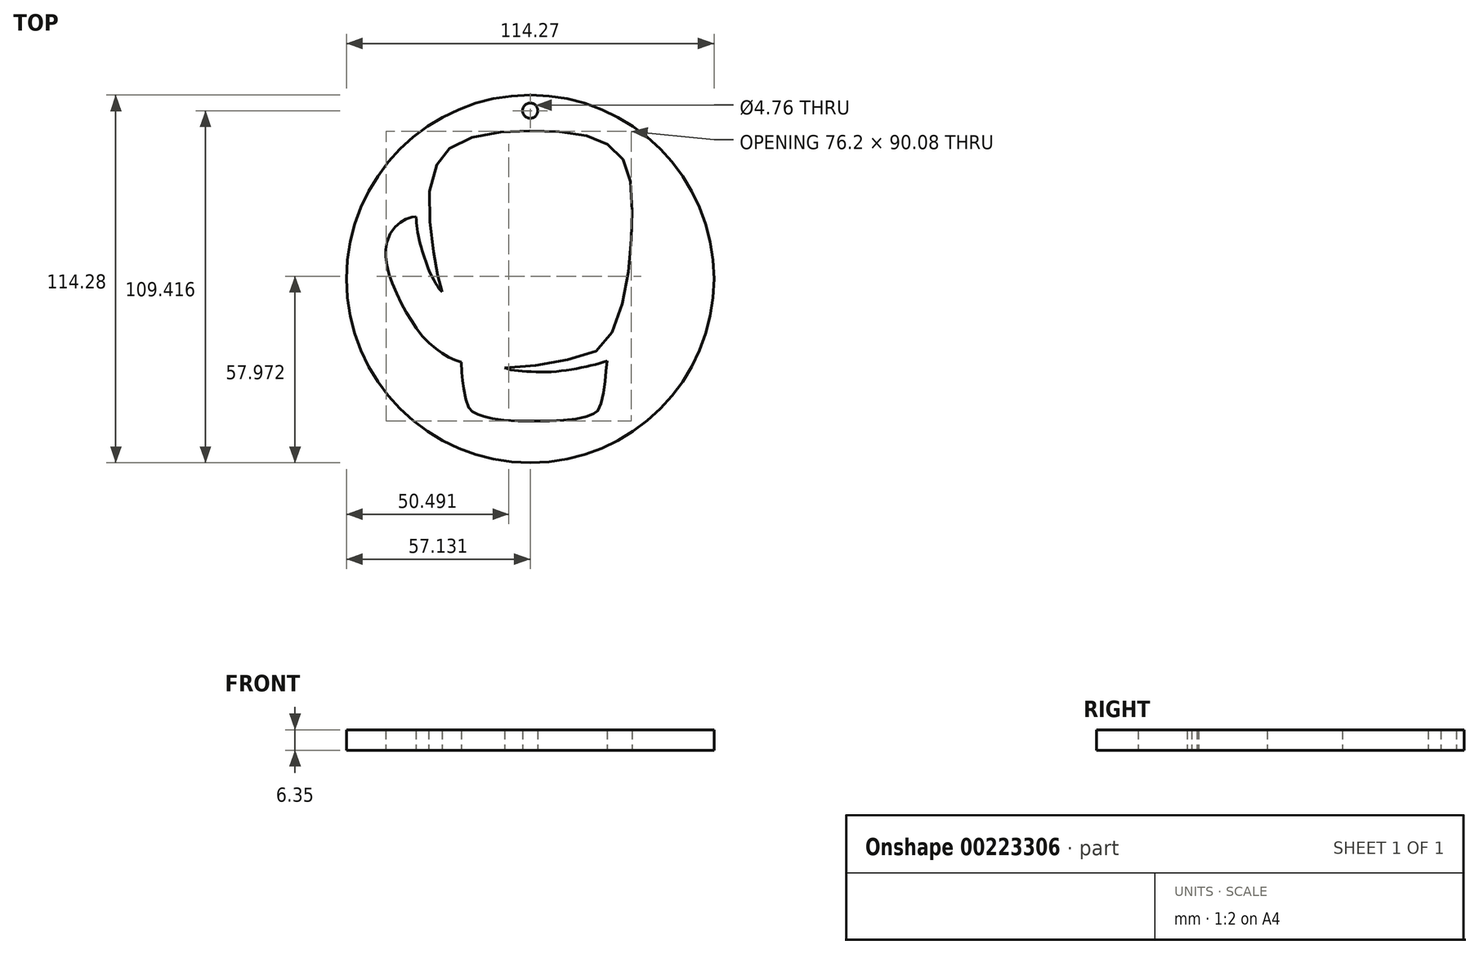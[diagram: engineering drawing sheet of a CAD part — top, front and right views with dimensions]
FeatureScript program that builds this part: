
annotation { "Feature Type Name" : "Feature", "Feature Type Description" : "" }
export const myFeature = defineFeature(function(context is Context, id is Id, definition is map)
    precondition{}
    {
        {
            var Q0;
            Q0=qCreatedBy(makeId("Top.planeOp"),FACE);
            var sketch = newSketch(context, id + "F0", { "sketchPlane" : qUnion([Q0])});
            skFitSpline(sketch, "E0", {"points": [v(-19.83, -27.64) * mm, v(-16.82, -28.45) * mm, v(-12.35, -28.83) * mm, v(-5.72, -28.9) * mm, v(1.21, -28.08) * mm, v(7.55, -26.81) * mm, v(12.02, -25.47) * mm], "startDerivative": vector(17.29, -8.64) * mm, "endDerivative": vector(27.03, 8.83) * mm});
            skFitSpline(sketch, "E1", {"points": [v(12.02, -25.47) * mm, v(11.52, -30.62) * mm, v(10.6, -36.69) * mm, v(9.34, -40.68) * mm, v(8.42, -41.6) * mm, v(6.65, -42.45) * mm, v(1.3, -43.69) * mm, v(-8.14, -44.22) * mm, v(-19.75, -43.9) * mm, v(-25.24, -43.07) * mm, v(-27.55, -42.4) * mm, v(-29.27, -41.56) * mm, v(-30.51, -40.72) * mm, v(-31.53, -38.6) * mm, v(-32.64, -33.36) * mm, v(-33, -30.44) * mm, v(-33.3, -25.93) * mm], "startDerivative": vector(-5.92, -73.94) * mm, "endDerivative": vector(-1.98, 80.2) * mm});
            skFitSpline(sketch, "E2", {"points": [v(-33.3, -25.93) * mm, v(-35.71, -25.04) * mm, v(-38.6, -23.54) * mm, v(-41.55, -21.45) * mm, v(-45.47, -17.7) * mm, v(-48.62, -13.22) * mm, v(-51.57, -8.28) * mm, v(-54.53, -1.8) * mm, v(-56.29, 3.44) * mm, v(-56.82, 7.75) * mm, v(-56.52, 10.97) * mm, v(-54.73, 15.08) * mm, v(-52.5, 17.3) * mm, v(-50.21, 18.74) * mm, v(-48.12, 19.27) * mm, v(-47.35, 19.26) * mm], "startDerivative": vector(-42.85, 14.66) * mm, "endDerivative": vector(20.25, -1.4) * mm});
            skFitSpline(sketch, "E3", {"points": [v(-47.35, 19.26) * mm, v(-47.23, 17.28) * mm, v(-46.89, 14.87) * mm, v(-46.24, 11.54) * mm, v(-45.35, 8.38) * mm, v(-44.33, 5.29) * mm, v(-42.94, 1.78) * mm, v(-41.1, -1.65) * mm, v(-40.08, -3.24) * mm, v(-39.3, -4.02) * mm], "startDerivative": vector(0.97, -20.52) * mm, "endDerivative": vector(11.11, -9.93) * mm});
            skFitSpline(sketch, "E4", {"points": [v(-39.3, -4.02) * mm, v(-39.64, -2.67) * mm, v(-40.4, 0) * mm, v(-40.97, 3.02) * mm, v(-41.79, 7.52) * mm, v(-42.61, 14.6) * mm, v(-43.35, 21.14) * mm, v(-42.98, 28.51) * mm, v(-41.35, 34.47) * mm, v(-39.68, 37.48) * mm, v(-37.55, 40.04) * mm, v(-34.2, 42.37) * mm, v(-28.98, 44.27) * mm, v(-22.63, 45.45) * mm, v(-16.36, 45.84) * mm, v(-9.33, 45.96) * mm, v(-2.74, 45.69) * mm, v(3.5, 44.98) * mm, v(7.87, 43.8) * mm, v(11.27, 42.3) * mm, v(14.62, 39.93) * mm, v(16.83, 37.32) * mm, v(18.45, 34.2) * mm, v(19.4, 29.2) * mm, v(19.75, 22.32) * mm, v(19.63, 16.37) * mm, v(19.36, 9.62) * mm, v(18.45, 1.17) * mm, v(17, -6.84) * mm, v(14.86, -13.82) * mm, v(11.9, -19.43) * mm, v(8.98, -22.23) * mm, v(2.94, -24.36) * mm, v(-4.28, -25.9) * mm, v(-12.8, -27.16) * mm, v(-19.83, -27.64) * mm], "startDerivative": vector(-19.55, 85.44) * mm, "endDerivative": vector(-208.2, -14.46) * mm});
            skSolve(sketch);
        }
        {
            var Q0;
            Q0=qCreatedBy(makeId("Top.planeOp"),FACE);
            var sketch = newSketch(context, id + "F1", { "sketchPlane" : qUnion([Q0])});
            skCircle(sketch, "E5", {"center": v(-11.87, 0) * mm, "radius": 57.14 * mm});
            skCircle(sketch, "E6", {"center": v(-11.87, 52.28) * mm, "radius": 2.38 * mm});
            skSolve(sketch);
        }
        {
            var Q0;
            Q0=makeQuery(id+"F1.imprint","IMPRINT",FACE,{"disambiguationData":[TD([[makeQuery(id+"F1.imprint","IMPRINT",EDGE,{"derivedFrom":sQuery(id+"F1.wireOp",EDGE,"E5")}),1.0]])]});
            extrude(context, id + "F2", {"entities" : qUnion([Q0]), "depth" : 6.35 * mm});
        }
        {
            var Q0;
            Q0 = qSketchRegion(id + "F0", true);
            extrude(context, id + "F3", {"entities" : qUnion([Q0]), "operationType" : NewBodyOperationType.REMOVE, "depth" : 6.35 * mm});
        }
    });
